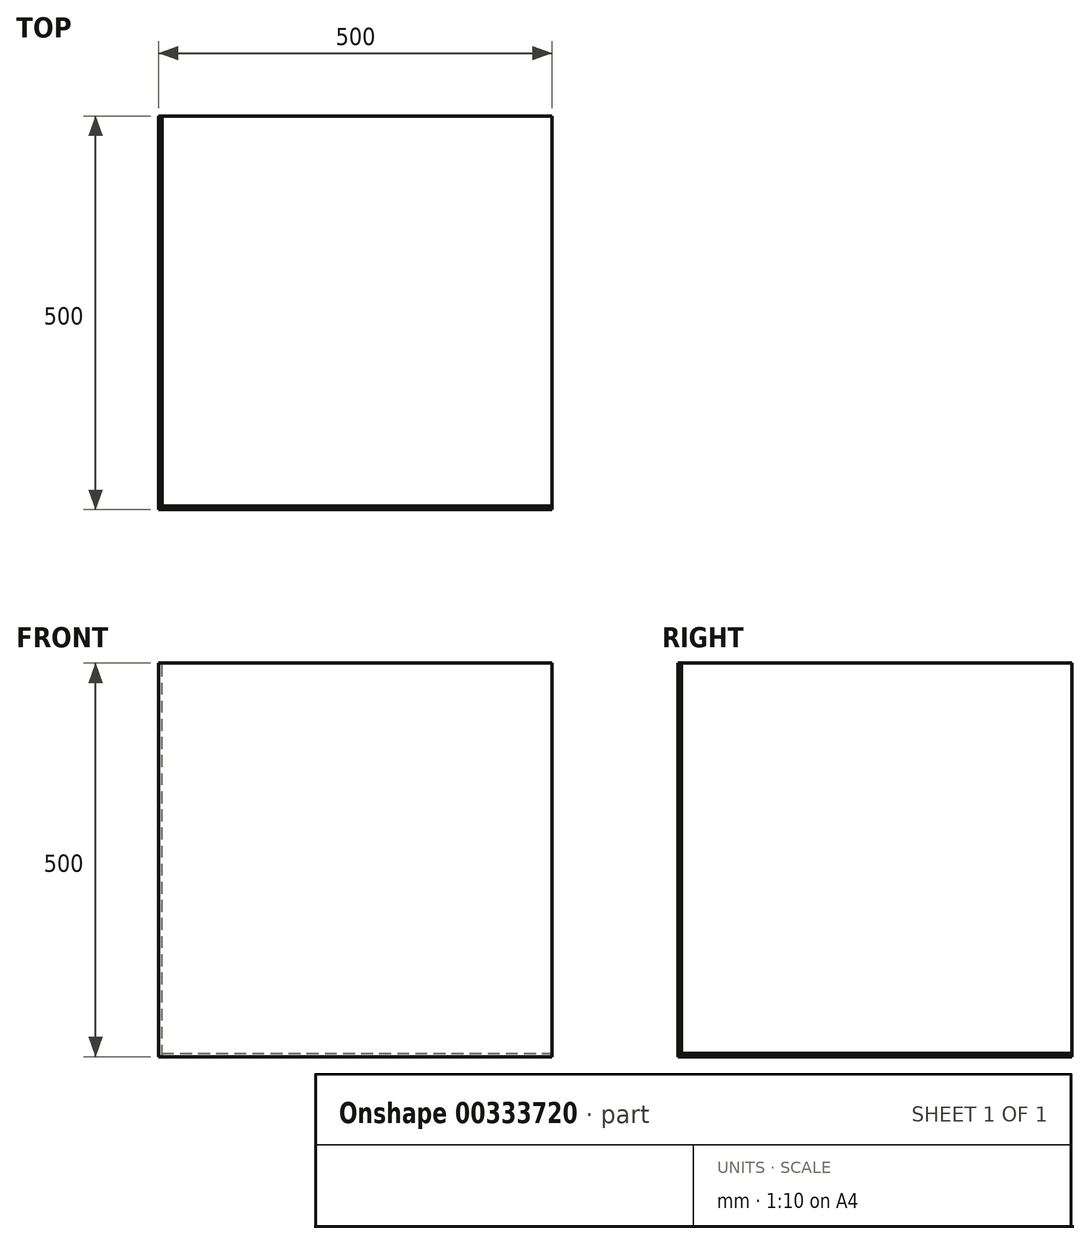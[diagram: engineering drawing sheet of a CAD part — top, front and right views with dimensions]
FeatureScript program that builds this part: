
annotation { "Feature Type Name" : "Feature", "Feature Type Description" : "" }
export const myFeature = defineFeature(function(context is Context, id is Id, definition is map)
    precondition{}
    {
        {
            var Q0;
            Q0=qCreatedBy(makeId("Top.planeOp"),FACE);
            var sketch = newSketch(context, id + "F0", { "sketchPlane" : qUnion([Q0])});
            skLineSegment(sketch, "E0", {"start": v(0, 0) * mm, "end": v(0, 500) * mm});
            skLineSegment(sketch, "E1", {"start": v(0, 500) * mm, "end": v(500, 0) * mm});
            skLineSegment(sketch, "E2", {"start": v(500, 0) * mm, "end": v(0, 0) * mm});
            skSolve(sketch);
        }
        {
            var Q0;
            Q0=qCreatedBy(makeId("Right.planeOp"),FACE);
            var sketch = newSketch(context, id + "F1", { "sketchPlane" : qUnion([Q0])});
            skLineSegment(sketch, "E3.bottom", {"start": v(0, 0) * mm, "end": v(500, 0) * mm});
            skLineSegment(sketch, "E3.top", {"start": v(0, 500) * mm, "end": v(500, 500) * mm});
            skLineSegment(sketch, "E3.left", {"start": v(0, 0) * mm, "end": v(0, 500) * mm});
            skLineSegment(sketch, "E3.right", {"start": v(500, 0) * mm, "end": v(500, 500) * mm});
            skSolve(sketch);
        }
        {
            var Q0;
            Q0 = qSketchRegion(id + "F1", true);
            extrude(context, id + "F2", {"entities" : qUnion([Q0]), "depth" : 4.25 * mm, "offsetDistance" : 25 * mm});
        }
        {
            var Q0;
            Q0=qCreatedBy(makeId("Front.planeOp"),FACE);
            var sketch = newSketch(context, id + "F3", { "sketchPlane" : qUnion([Q0])});
            skLineSegment(sketch, "E4.bottom", {"start": v(0, 0) * mm, "end": v(500, 0) * mm});
            skLineSegment(sketch, "E4.top", {"start": v(0, 500) * mm, "end": v(500, 500) * mm});
            skLineSegment(sketch, "E4.left", {"start": v(0, 0) * mm, "end": v(0, 500) * mm});
            skLineSegment(sketch, "E4.right", {"start": v(500, 0) * mm, "end": v(500, 500) * mm});
            skSolve(sketch);
        }
        {
            var Q0;
            Q0 = qSketchRegion(id + "F3", true);
            extrude(context, id + "F4", {"entities" : qUnion([Q0]), "oppositeDirection" : true, "depth" : 4.25 * mm, "offsetDistance" : 25 * mm});
        }
        {
            var Q0;
            Q0=makeQuery(id+"F2.opExtrude","CAP_EDGE",EDGE,{"disambiguationData":[OSD([sQuery(id+"F1.wireOp",EDGE,"E3.left")])],"isStart":false});
            var Q1;
            Q1=makeQuery(id+"F4.opExtrude","CAP_EDGE",EDGE,{"disambiguationData":[OSD([sQuery(id+"F3.wireOp",EDGE,"E4.left")])],"isStart":false});
            chamfer(context, id + "F5", {"entities" : qUnion([Q0, Q1]), "width" : 4.25 * mm, "tangentPropagation" : true});
        }
        {
            var Q0;
            Q0=makeQuery(id+"F4.opExtrude","SWEPT_FACE",FACE,{"disambiguationData":[OSD([sQuery(id+"F3.wireOp",EDGE,"E4.bottom")])]});
            var sketch = newSketch(context, id + "F6", { "sketchPlane" : qUnion([Q0])});
            skLineSegment(sketch, "E5.bottom", {"start": v(4.25, -4.25) * mm, "end": v(500, -4.25) * mm});
            skLineSegment(sketch, "E5.top", {"start": v(4.25, -500) * mm, "end": v(500, -500) * mm});
            skLineSegment(sketch, "E5.left", {"start": v(4.25, -4.25) * mm, "end": v(4.25, -500) * mm});
            skLineSegment(sketch, "E5.right", {"start": v(500, -4.25) * mm, "end": v(500, -500) * mm});
            skSolve(sketch);
        }
        {
            var Q0;
            Q0 = qSketchRegion(id + "F6", true);
            extrude(context, id + "F7", {"entities" : qUnion([Q0]), "oppositeDirection" : true, "depth" : 4.25 * mm, "offsetDistance" : 25 * mm});
        }
    });
